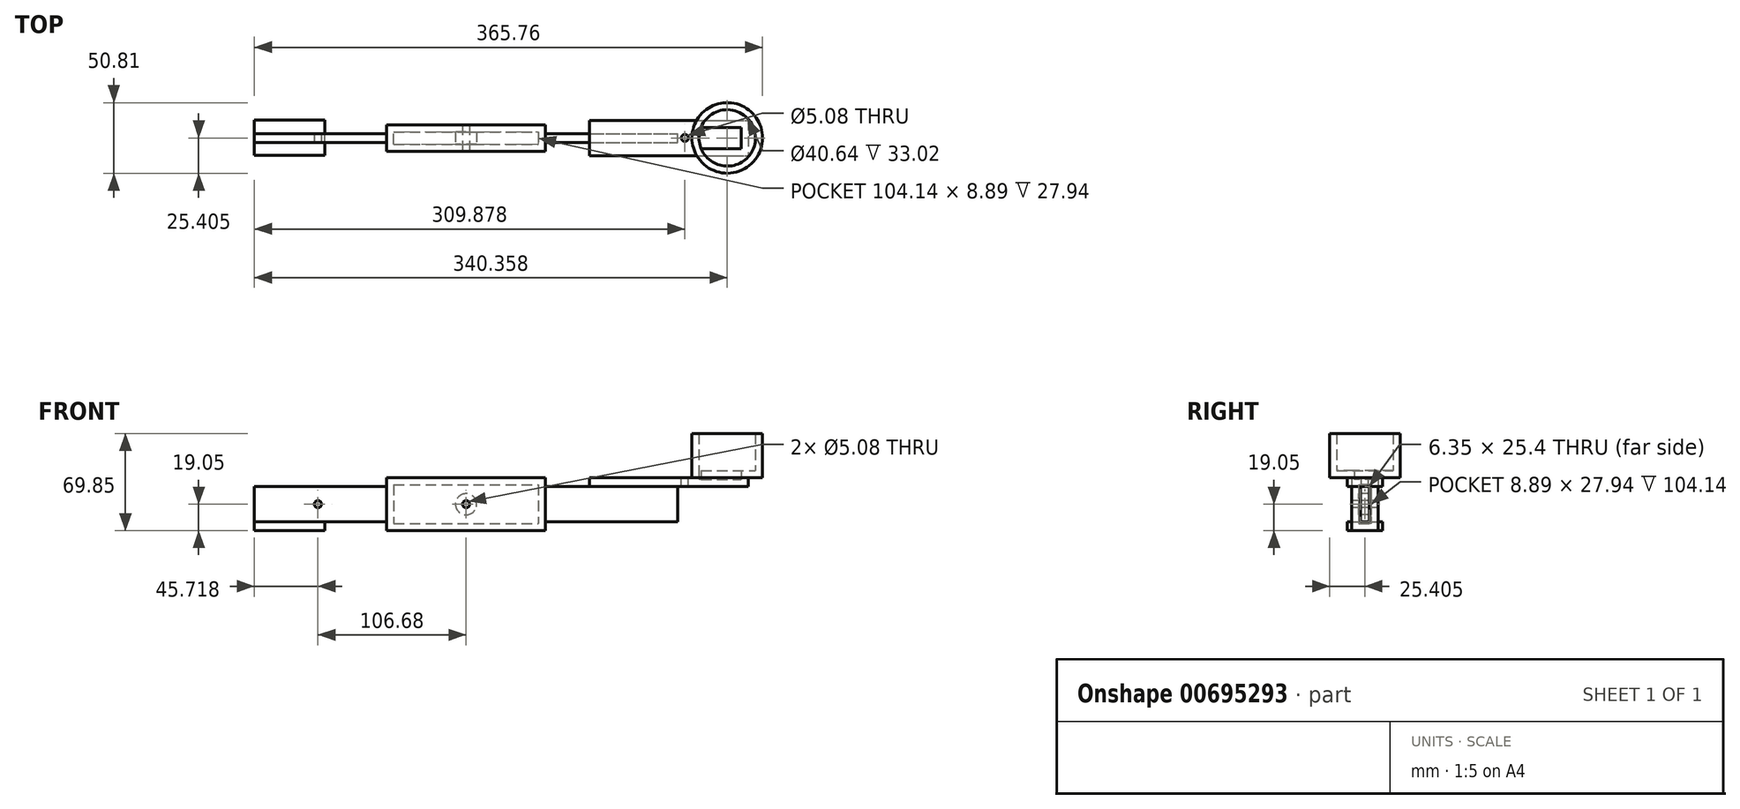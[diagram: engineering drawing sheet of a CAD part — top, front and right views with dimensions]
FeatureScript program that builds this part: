
annotation { "Feature Type Name" : "Feature", "Feature Type Description" : "" }
export const myFeature = defineFeature(function(context is Context, id is Id, definition is map)
    precondition{}
    {
        {
            var Q0;
            Q0=qCreatedBy(makeId("Front.planeOp"),FACE);
            var sketch = newSketch(context, id + "F0", { "sketchPlane" : qUnion([Q0])});
            skLineSegment(sketch, "E0.bottom", {"start": v(-35.42, 25.4) * mm, "end": v(269.38, 25.4) * mm});
            skLineSegment(sketch, "E0.top", {"start": v(-35.42, 0) * mm, "end": v(269.38, 0) * mm});
            skLineSegment(sketch, "E0.left", {"start": v(-35.42, 25.4) * mm, "end": v(-35.42, 0) * mm});
            skLineSegment(sketch, "E0.right", {"start": v(269.38, 25.4) * mm, "end": v(269.38, 0) * mm});
            skSolve(sketch);
        }
        {
            var Q0;
            Q0 = qSketchRegion(id + "F0", true);
            extrude(context, id + "F1", {"entities" : qUnion([Q0]), "depth" : 6.35 * mm, "offsetDistance" : 25.4 * mm});
        }
        {
            var Q0;
            Q0=makeQuery(id+"F1.opExtrude","CAP_FACE",FACE,{"disambiguationData":[OSD([sQuery(id+"F0.wireOp",EDGE,"E0.bottom"),sQuery(id+"F0.wireOp",EDGE,"E0.top"),sQuery(id+"F0.wireOp",EDGE,"E0.left"),sQuery(id+"F0.wireOp",EDGE,"E0.right")])],"isStart":false});
            var sketch = newSketch(context, id + "F2", { "sketchPlane" : qUnion([Q0])});
            skLineSegment(sketch, "E1.bottom", {"start": v(59.83, 25.4) * mm, "end": v(174.13, 25.4) * mm});
            skLineSegment(sketch, "E1.top", {"start": v(59.83, 0) * mm, "end": v(174.13, 0) * mm});
            skLineSegment(sketch, "E1.left", {"start": v(59.83, 25.4) * mm, "end": v(59.83, 0) * mm});
            skLineSegment(sketch, "E1.right", {"start": v(174.13, 25.4) * mm, "end": v(174.13, 0) * mm});
            skSolve(sketch);
        }
        {
            var Q0;
            Q0=makeQuery(id+"F2.imprint","IMPRINT",FACE,{"disambiguationData":[TD([[makeQuery(id+"F2.imprint","IMPRINT",EDGE,{"derivedFrom":sQuery(id+"F2.wireOp",EDGE,"E1.bottom")}),-1.0]])]});
            extrude(context, id + "F3", {"entities" : qUnion([Q0]), "operationType" : NewBodyOperationType.ADD, "depth" : 6.35 * mm, "offsetDistance" : 25.4 * mm});
        }
        {
            var Q0;
            Q0=makeQuery(id+"F1.opExtrude","CAP_FACE",FACE,{"disambiguationData":[OSD([sQuery(id+"F0.wireOp",EDGE,"E0.bottom"),sQuery(id+"F0.wireOp",EDGE,"E0.top"),sQuery(id+"F0.wireOp",EDGE,"E0.left"),sQuery(id+"F0.wireOp",EDGE,"E0.right")])],"isStart":true});
            var sketch = newSketch(context, id + "F4", { "sketchPlane" : qUnion([Q0])});
            skLineSegment(sketch, "E2.bottom", {"start": v(-59.83, 25.4) * mm, "end": v(-174.13, 25.4) * mm});
            skLineSegment(sketch, "E2.top", {"start": v(-59.83, 0) * mm, "end": v(-174.13, 0) * mm});
            skLineSegment(sketch, "E2.left", {"start": v(-59.83, 25.4) * mm, "end": v(-59.83, 0) * mm});
            skLineSegment(sketch, "E2.right", {"start": v(-174.13, 25.4) * mm, "end": v(-174.13, 0) * mm});
            skSolve(sketch);
        }
        {
            var Q0;
            Q0=makeQuery(id+"F4.imprint","IMPRINT",FACE,{"disambiguationData":[TD([[makeQuery(id+"F4.imprint","IMPRINT",EDGE,{"derivedFrom":sQuery(id+"F4.wireOp",EDGE,"E2.bottom")}),1.0]])]});
            extrude(context, id + "F5", {"entities" : qUnion([Q0]), "operationType" : NewBodyOperationType.ADD, "depth" : 6.35 * mm, "offsetDistance" : 25.4 * mm});
        }
        {
            var Q0;
            {var subQ0=sQuery(id+"F0.wireOp",EDGE,"E0.left");var subQ1=sQuery(id+"F0.wireOp",EDGE,"E0.top");var subQ2=sQuery(id+"F0.wireOp",EDGE,"E0.bottom");Q0=makeQuery(id+"F3.boolean.opBoolean","SPLIT",FACE,{"disambiguationData":[TD([makeQuery(id+"F1.opExtrude","SWEPT_FACE",FACE,{"disambiguationData":[OSD([subQ0])]})])],"derivedFrom":makeQuery(id+"F1.opExtrude","CAP_FACE",FACE,{"disambiguationData":[OSD([subQ2,subQ1,subQ0,sQuery(id+"F0.wireOp",EDGE,"E0.right")])],"isStart":false})});}
            var sketch = newSketch(context, id + "F6", { "sketchPlane" : qUnion([Q0])});
            skCircle(sketch, "E3", {"center": v(10.3, 12.7) * mm, "radius": 2.54 * mm});
            skSolve(sketch);
        }
        {
            var Q0;
            Q0=sQuery(id+"F6.wireOp",VERTEX,"E3.center");
            var Q1;
            Q1=makeQuery(id+"F1.opExtrude","SWEPT_BODY",BODY,{"disambiguationData":[OSD([sQuery(id+"F0.wireOp",EDGE,"E0.bottom"),sQuery(id+"F0.wireOp",EDGE,"E0.top"),sQuery(id+"F0.wireOp",EDGE,"E0.left"),sQuery(id+"F0.wireOp",EDGE,"E0.right")])]});
            hole(context, id + "F7", {"style" : HoleStyle.SIMPLE, "endStyle" : HoleEndStyle.THROUGH, "holeDiameter" : 5.08 * mm, "majorDiameter" : 6.35 * mm, "isTappedThrough" : true, "tappedDepth" : 12.7 * mm, "tapClearance" : 3, "locations" : qUnion([Q0]), "scope" : qUnion([Q1])});
        }
        {
            var Q0;
            Q0=makeQuery(id+"F3.opExtrude","CAP_FACE",FACE,{"disambiguationData":[OSD([sQuery(id+"F2.wireOp",EDGE,"E1.bottom"),sQuery(id+"F2.wireOp",EDGE,"E1.top"),sQuery(id+"F2.wireOp",EDGE,"E1.left"),sQuery(id+"F2.wireOp",EDGE,"E1.right")])],"isStart":false});
            var sketch = newSketch(context, id + "F8", { "sketchPlane" : qUnion([Q0])});
            skCircle(sketch, "E4", {"center": v(116.98, 12.7) * mm, "radius": 2.54 * mm});
            skSolve(sketch);
        }
        {
            var Q0;
            Q0=sQuery(id+"F8.wireOp",VERTEX,"E4.center");
            var Q1;
            Q1=makeQuery(id+"F1.opExtrude","SWEPT_BODY",BODY,{"disambiguationData":[OSD([sQuery(id+"F0.wireOp",EDGE,"E0.bottom"),sQuery(id+"F0.wireOp",EDGE,"E0.top"),sQuery(id+"F0.wireOp",EDGE,"E0.left"),sQuery(id+"F0.wireOp",EDGE,"E0.right")])]});
            hole(context, id + "F9", {"style" : HoleStyle.SIMPLE, "endStyle" : HoleEndStyle.THROUGH, "holeDiameter" : 5.08 * mm, "majorDiameter" : 6.35 * mm, "isTappedThrough" : true, "tappedDepth" : 12.7 * mm, "tapClearance" : 3, "locations" : qUnion([Q0]), "scope" : qUnion([Q1])});
        }
        {
            var Q0;
            Q0=makeQuery(id+"F5.boolean.opBoolean","MERGE",FACE,{"derivedFrom":[makeQuery(id+"F3.boolean.opBoolean","MERGE",FACE,{"derivedFrom":[makeQuery(id+"F1.opExtrude","SWEPT_FACE",FACE,{"disambiguationData":[OSD([sQuery(id+"F0.wireOp",EDGE,"E0.bottom")])]}),makeQuery(id+"F3.opExtrude","SWEPT_FACE",FACE,{"disambiguationData":[OSD([sQuery(id+"F2.wireOp",EDGE,"E1.bottom")])]})]}),makeQuery(id+"F5.opExtrude","SWEPT_FACE",FACE,{"disambiguationData":[OSD([sQuery(id+"F4.wireOp",EDGE,"E2.bottom")])]})]});
            var sketch = newSketch(context, id + "F10", { "sketchPlane" : qUnion([Q0])});
            skLineSegment(sketch, "E5.bottom", {"start": v(59.83, 6.35) * mm, "end": v(174.13, 6.35) * mm});
            skLineSegment(sketch, "E5.top", {"start": v(59.83, -12.7) * mm, "end": v(174.13, -12.7) * mm});
            skLineSegment(sketch, "E5.left", {"start": v(59.83, 6.35) * mm, "end": v(59.83, -12.7) * mm});
            skLineSegment(sketch, "E5.right", {"start": v(174.13, 6.35) * mm, "end": v(174.13, -12.7) * mm});
            skSolve(sketch);
        }
        {
            var Q0;
            Q0 = qSketchRegion(id + "F10", true);
            extrude(context, id + "F11", {"entities" : qUnion([Q0]), "operationType" : NewBodyOperationType.ADD, "depth" : 6.35 * mm, "offsetDistance" : 25.4 * mm});
        }
        {
            var Q0;
            Q0=makeQuery(id+"F5.boolean.opBoolean","MERGE",FACE,{"derivedFrom":[makeQuery(id+"F3.boolean.opBoolean","MERGE",FACE,{"derivedFrom":[makeQuery(id+"F1.opExtrude","SWEPT_FACE",FACE,{"disambiguationData":[OSD([sQuery(id+"F0.wireOp",EDGE,"E0.top")])]}),makeQuery(id+"F3.opExtrude","SWEPT_FACE",FACE,{"disambiguationData":[OSD([sQuery(id+"F2.wireOp",EDGE,"E1.top")])]})]}),makeQuery(id+"F5.opExtrude","SWEPT_FACE",FACE,{"disambiguationData":[OSD([sQuery(id+"F4.wireOp",EDGE,"E2.top")])]})]});
            var sketch = newSketch(context, id + "F12", { "sketchPlane" : qUnion([Q0])});
            skLineSegment(sketch, "E6.bottom", {"start": v(59.83, 12.7) * mm, "end": v(174.13, 12.7) * mm});
            skLineSegment(sketch, "E6.top", {"start": v(59.83, -6.35) * mm, "end": v(174.13, -6.35) * mm});
            skLineSegment(sketch, "E6.left", {"start": v(59.83, 12.7) * mm, "end": v(59.83, -6.35) * mm});
            skLineSegment(sketch, "E6.right", {"start": v(174.13, 12.7) * mm, "end": v(174.13, -6.35) * mm});
            skSolve(sketch);
        }
        {
            var Q0;
            {var subQ16=sQuery(id+"F12.wireOp",EDGE,"E6.bottom");Q0=makeQuery(id+"F12.imprint","IMPRINT",FACE,{"disambiguationData":[TD([[makeQuery(id+"F12.imprint","IMPRINT",EDGE,{"derivedFrom":subQ16}),-1.0]])]});}
            extrude(context, id + "F13", {"entities" : qUnion([Q0]), "operationType" : NewBodyOperationType.ADD, "depth" : 6.35 * mm, "offsetDistance" : 25.4 * mm});
        }
        {
            var Q0;
            {var subQ0=sQuery(id+"F0.wireOp",EDGE,"E0.left");var subQ2=sQuery(id+"F0.wireOp",EDGE,"E0.top");Q0=makeQuery(id+"F13.boolean.opBoolean","SPLIT",FACE,{"disambiguationData":[TD([makeQuery(id+"F1.opExtrude","SWEPT_FACE",FACE,{"disambiguationData":[OSD([subQ0])]})])],"derivedFrom":makeQuery(id+"F5.boolean.opBoolean","MERGE",FACE,{"derivedFrom":[makeQuery(id+"F3.boolean.opBoolean","MERGE",FACE,{"derivedFrom":[makeQuery(id+"F1.opExtrude","SWEPT_FACE",FACE,{"disambiguationData":[OSD([subQ2])]}),makeQuery(id+"F3.opExtrude","SWEPT_FACE",FACE,{"disambiguationData":[OSD([sQuery(id+"F2.wireOp",EDGE,"E1.top")])]})]}),makeQuery(id+"F5.opExtrude","SWEPT_FACE",FACE,{"disambiguationData":[OSD([sQuery(id+"F4.wireOp",EDGE,"E2.top")])]})]})});}
            var sketch = newSketch(context, id + "F14", { "sketchPlane" : qUnion([Q0])});
            skLineSegment(sketch, "E7.bottom", {"start": v(-35.42, 15.75) * mm, "end": v(15.38, 15.75) * mm});
            skLineSegment(sketch, "E7.top", {"start": v(-35.42, -9.65) * mm, "end": v(15.38, -9.65) * mm});
            skLineSegment(sketch, "E7.left", {"start": v(-35.42, 15.75) * mm, "end": v(-35.42, -9.65) * mm});
            skLineSegment(sketch, "E7.right", {"start": v(15.38, 15.75) * mm, "end": v(15.38, -9.65) * mm});
            skSolve(sketch);
        }
        {
            var Q0;
            {var subQ0=sQuery(id+"F14.wireOp",EDGE,"E7.bottom");Q0=makeQuery(id+"F14.imprint","IMPRINT",FACE,{"disambiguationData":[TD([[makeQuery(id+"F14.imprint","IMPRINT",EDGE,{"derivedFrom":subQ0}),-1.0]])]});}
            var Q1;
            {var subQ0=sQuery(id+"F14.wireOp",EDGE,"E7.top");Q1=makeQuery(id+"F14.imprint","IMPRINT",FACE,{"disambiguationData":[TD([[makeQuery(id+"F14.imprint","IMPRINT",EDGE,{"derivedFrom":subQ0}),1.0]])]});}
            var Q2;
            {var subQ0=sQuery(id+"F14.wireOp",EDGE,"E7.left");var subQ1=sQuery(id+"F0.wireOp",EDGE,"E0.left");var subQ2=makeQuery(id+"F1.opExtrude","SWEPT_FACE",FACE,{"disambiguationData":[OSD([subQ1])]});var subQ4=sQuery(id+"F0.wireOp",EDGE,"E0.top");var subQ10=makeQuery(id+"F3.boolean.opBoolean","SPLIT",EDGE,{"disambiguationData":[TD([subQ2])],"derivedFrom":makeQuery(id+"F1.opExtrude","CAP_EDGE",EDGE,{"disambiguationData":[OSD([subQ4])],"isStart":false})});var subQ11=makeQuery(id+"F14.imprint","INTERSECT",VERTEX,{"derivedFrom":[subQ10,subQ0]});Q2=makeQuery(id+"F14.imprint","IMPRINT",FACE,{"disambiguationData":[TD([[makeQuery(id+"F14.imprint","IMPRINT",EDGE,{"disambiguationData":[TD([[subQ11,-1.0]])],"derivedFrom":subQ0}),1.0]])]});}
            extrude(context, id + "F15", {"entities" : qUnion([Q0, Q1, Q2]), "operationType" : NewBodyOperationType.ADD, "depth" : 6.35 * mm, "offsetDistance" : 25.4 * mm});
        }
        {
            var Q0;
            {var subQ0=sQuery(id+"F0.wireOp",EDGE,"E0.right");var subQ3=sQuery(id+"F0.wireOp",EDGE,"E0.bottom");Q0=makeQuery(id+"F11.boolean.opBoolean","SPLIT",FACE,{"disambiguationData":[TD([makeQuery(id+"F1.opExtrude","SWEPT_FACE",FACE,{"disambiguationData":[OSD([subQ0])]})])],"derivedFrom":makeQuery(id+"F5.boolean.opBoolean","MERGE",FACE,{"derivedFrom":[makeQuery(id+"F3.boolean.opBoolean","MERGE",FACE,{"derivedFrom":[makeQuery(id+"F1.opExtrude","SWEPT_FACE",FACE,{"disambiguationData":[OSD([subQ3])]}),makeQuery(id+"F3.opExtrude","SWEPT_FACE",FACE,{"disambiguationData":[OSD([sQuery(id+"F2.wireOp",EDGE,"E1.bottom")])]})]}),makeQuery(id+"F5.opExtrude","SWEPT_FACE",FACE,{"disambiguationData":[OSD([sQuery(id+"F4.wireOp",EDGE,"E2.bottom")])]})]})});}
            var sketch = newSketch(context, id + "F16", { "sketchPlane" : qUnion([Q0])});
            skLineSegment(sketch, "E8.bottom", {"start": v(205.88, 9.53) * mm, "end": v(320.18, 9.53) * mm});
            skLineSegment(sketch, "E8.top", {"start": v(205.88, -15.88) * mm, "end": v(320.18, -15.88) * mm});
            skLineSegment(sketch, "E8.left", {"start": v(205.88, 9.53) * mm, "end": v(205.88, -15.88) * mm});
            skLineSegment(sketch, "E8.right", {"start": v(320.18, 9.53) * mm, "end": v(320.18, -15.88) * mm});
            skSolve(sketch);
        }
        {
            var Q0;
            {var subQ11=sQuery(id+"F16.wireOp",EDGE,"E8.bottom");Q0=makeQuery(id+"F16.imprint","IMPRINT",FACE,{"disambiguationData":[TD([[makeQuery(id+"F16.imprint","IMPRINT",EDGE,{"derivedFrom":subQ11}),-1.0]])]});}
            var Q1;
            {var subQ2=sQuery(id+"F0.wireOp",EDGE,"E0.right");var subQ5=sQuery(id+"F0.wireOp",EDGE,"E0.bottom");var subQ12=makeQuery(id+"F1.opExtrude","SWEPT_EDGE",EDGE,{"disambiguationData":[OSD([subQ5,subQ2])]});Q1=makeQuery(id+"F16.imprint","IMPRINT",FACE,{"disambiguationData":[TD([[makeQuery(id+"F16.imprint","IMPRINT",EDGE,{"derivedFrom":subQ12}),1.0]])]});}
            extrude(context, id + "F17", {"entities" : qUnion([Q0, Q1]), "operationType" : NewBodyOperationType.ADD, "depth" : 6.35 * mm, "offsetDistance" : 25.4 * mm});
        }
        {
            var Q0;
            Q0=makeQuery(id+"F17.opExtrude","CAP_FACE",FACE,{"disambiguationData":[OSD([sQuery(id+"F16.wireOp",EDGE,"E8.bottom"),sQuery(id+"F16.wireOp",EDGE,"E8.top"),sQuery(id+"F16.wireOp",EDGE,"E8.left"),sQuery(id+"F16.wireOp",EDGE,"E8.right")])],"isStart":false});
            var sketch = newSketch(context, id + "F18", { "sketchPlane" : qUnion([Q0])});
            skCircle(sketch, "E9", {"center": v(274.46, -3.17) * mm, "radius": 2.54 * mm});
            skSolve(sketch);
        }
        {
            var Q0;
            Q0=sQuery(id+"F18.wireOp",VERTEX,"E9.center");
            var Q1;
            Q1=makeQuery(id+"F1.opExtrude","SWEPT_BODY",BODY,{"disambiguationData":[OSD([sQuery(id+"F0.wireOp",EDGE,"E0.bottom"),sQuery(id+"F0.wireOp",EDGE,"E0.top"),sQuery(id+"F0.wireOp",EDGE,"E0.left"),sQuery(id+"F0.wireOp",EDGE,"E0.right")])]});
            hole(context, id + "F19", {"style" : HoleStyle.SIMPLE, "endStyle" : HoleEndStyle.THROUGH, "holeDiameter" : 5.08 * mm, "majorDiameter" : 6.35 * mm, "isTappedThrough" : true, "tappedDepth" : 12.7 * mm, "tapClearance" : 3, "locations" : qUnion([Q0]), "scope" : qUnion([Q1])});
        }
        {
            var Q0;
            Q0=makeQuery(id+"F17.opExtrude","CAP_FACE",FACE,{"disambiguationData":[OSD([sQuery(id+"F16.wireOp",EDGE,"E8.bottom"),sQuery(id+"F16.wireOp",EDGE,"E8.top"),sQuery(id+"F16.wireOp",EDGE,"E8.left"),sQuery(id+"F16.wireOp",EDGE,"E8.right")])],"isStart":false});
            var sketch = newSketch(context, id + "F20", { "sketchPlane" : qUnion([Q0])});
            skCircle(sketch, "E10", {"center": v(304.94, -3.17) * mm, "radius": 25.4 * mm});
            skSolve(sketch);
        }
        {
            var Q0;
            {var subQ5=makeQuery(id+"F17.opExtrude","CAP_EDGE",EDGE,{"disambiguationData":[OSD([sQuery(id+"F16.wireOp",EDGE,"E8.right")])],"isStart":false});Q0=makeQuery(id+"F20.imprint","IMPRINT",FACE,{"disambiguationData":[TD([[makeQuery(id+"F20.imprint","IMPRINT",EDGE,{"derivedFrom":subQ5}),1.0]])]});}
            var Q1;
            {var subQ5=makeQuery(id+"F17.opExtrude","CAP_EDGE",EDGE,{"disambiguationData":[OSD([sQuery(id+"F16.wireOp",EDGE,"E8.right")])],"isStart":false});Q1=makeQuery(id+"F20.imprint","IMPRINT",FACE,{"disambiguationData":[TD([[makeQuery(id+"F20.imprint","IMPRINT",EDGE,{"derivedFrom":subQ5}),-1.0]])]});}
            extrude(context, id + "F21", {"entities" : qUnion([Q0, Q1]), "operationType" : NewBodyOperationType.ADD, "depth" : 31.75 * mm, "offsetDistance" : 25.4 * mm});
        }
        {
            var Q0;
            Q0=makeQuery(id+"F21.opExtrude","CAP_FACE",FACE,{"disambiguationData":[OSD([sQuery(id+"F20.wireOp",EDGE,"E10")])],"isStart":false});
            shell(context, id + "F22", {"entities" : qUnion([Q0]), "thickness" : 5.08 * mm});
        }
    });
